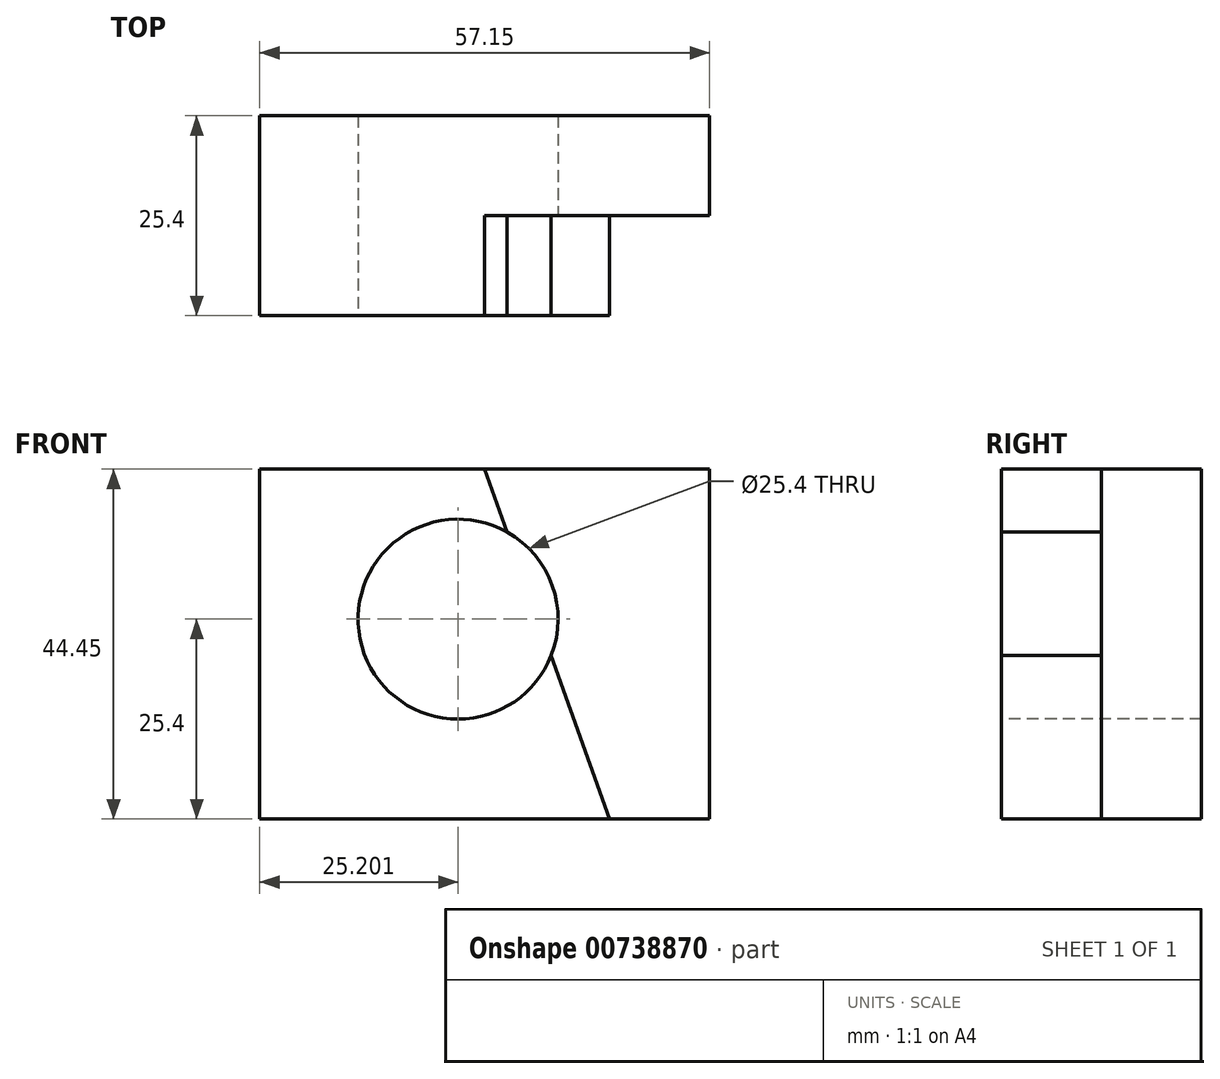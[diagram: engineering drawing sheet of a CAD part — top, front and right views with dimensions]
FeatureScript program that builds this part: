
annotation { "Feature Type Name" : "Feature", "Feature Type Description" : "" }
export const myFeature = defineFeature(function(context is Context, id is Id, definition is map)
    precondition{}
    {
        {
            var Q0;
            Q0=qCreatedBy(makeId("Front.planeOp"),FACE);
            var sketch = newSketch(context, id + "F0", { "sketchPlane" : qUnion([Q0])});
            skLineSegment(sketch, "E0", {"start": v(0, 44.45) * mm, "end": v(0, 0) * mm});
            skLineSegment(sketch, "E1", {"start": v(0, 0) * mm, "end": v(57.15, 0) * mm});
            skLineSegment(sketch, "E2", {"start": v(57.15, 0) * mm, "end": v(57.15, 44.45) * mm});
            skLineSegment(sketch, "E3", {"start": v(57.15, 44.45) * mm, "end": v(0, 44.45) * mm});
            skSolve(sketch);
        }
        {
            var Q0;
            Q0 = qSketchRegion(id + "F0", true);
            extrude(context, id + "F1", {"entities" : qUnion([Q0]), "depth" : 25.4 * mm, "offsetDistance" : 25.4 * mm});
        }
        {
            var Q0;
            Q0=makeQuery(id+"F1.opExtrude","CAP_FACE",FACE,{"disambiguationData":[OSD([sQuery(id+"F0.wireOp",EDGE,"E0"),sQuery(id+"F0.wireOp",EDGE,"E1"),sQuery(id+"F0.wireOp",EDGE,"E2"),sQuery(id+"F0.wireOp",EDGE,"E3")])],"isStart":false});
            var sketch = newSketch(context, id + "F2", { "sketchPlane" : qUnion([Q0])});
            skCircle(sketch, "E4", {"center": v(25.2, 25.4) * mm, "radius": 12.7 * mm});
            skSolve(sketch);
        }
        {
            var Q0;
            Q0=makeQuery(id+"F2.imprint","IMPRINT",FACE,{"disambiguationData":[TD([[makeQuery(id+"F2.imprint","IMPRINT",EDGE,{"derivedFrom":sQuery(id+"F2.wireOp",EDGE,"E4")}),1.0]])]});
            extrude(context, id + "F3", {"entities" : qUnion([Q0]), "operationType" : NewBodyOperationType.REMOVE, "endBound" : BoundingType.THROUGH_ALL, "oppositeDirection" : true, "depth" : 25.4 * mm, "offsetDistance" : 25.4 * mm});
        }
        {
            var Q0;
            Q0=makeQuery(id+"F1.opExtrude","CAP_FACE",FACE,{"disambiguationData":[OSD([sQuery(id+"F0.wireOp",EDGE,"E0"),sQuery(id+"F0.wireOp",EDGE,"E1"),sQuery(id+"F0.wireOp",EDGE,"E2"),sQuery(id+"F0.wireOp",EDGE,"E3")])],"isStart":false});
            var sketch = newSketch(context, id + "F4", { "sketchPlane" : qUnion([Q0])});
            skLineSegment(sketch, "E5", {"start": v(28.58, 44.45) * mm, "end": v(44.45, 0) * mm});
            skSolve(sketch);
        }
        {
            var Q0;
            {var subQ0=makeQuery(id+"F1.opExtrude","CAP_EDGE",EDGE,{"disambiguationData":[OSD([sQuery(id+"F0.wireOp",EDGE,"E2")])],"isStart":false});Q0=makeQuery(id+"F4.imprint","IMPRINT",FACE,{"disambiguationData":[TD([[makeQuery(id+"F4.imprint","IMPRINT",EDGE,{"derivedFrom":subQ0}),1.0]])]});}
            extrude(context, id + "F5", {"entities" : qUnion([Q0]), "operationType" : NewBodyOperationType.REMOVE, "oppositeDirection" : true, "depth" : 12.7 * mm, "offsetDistance" : 25.4 * mm});
        }
    });
